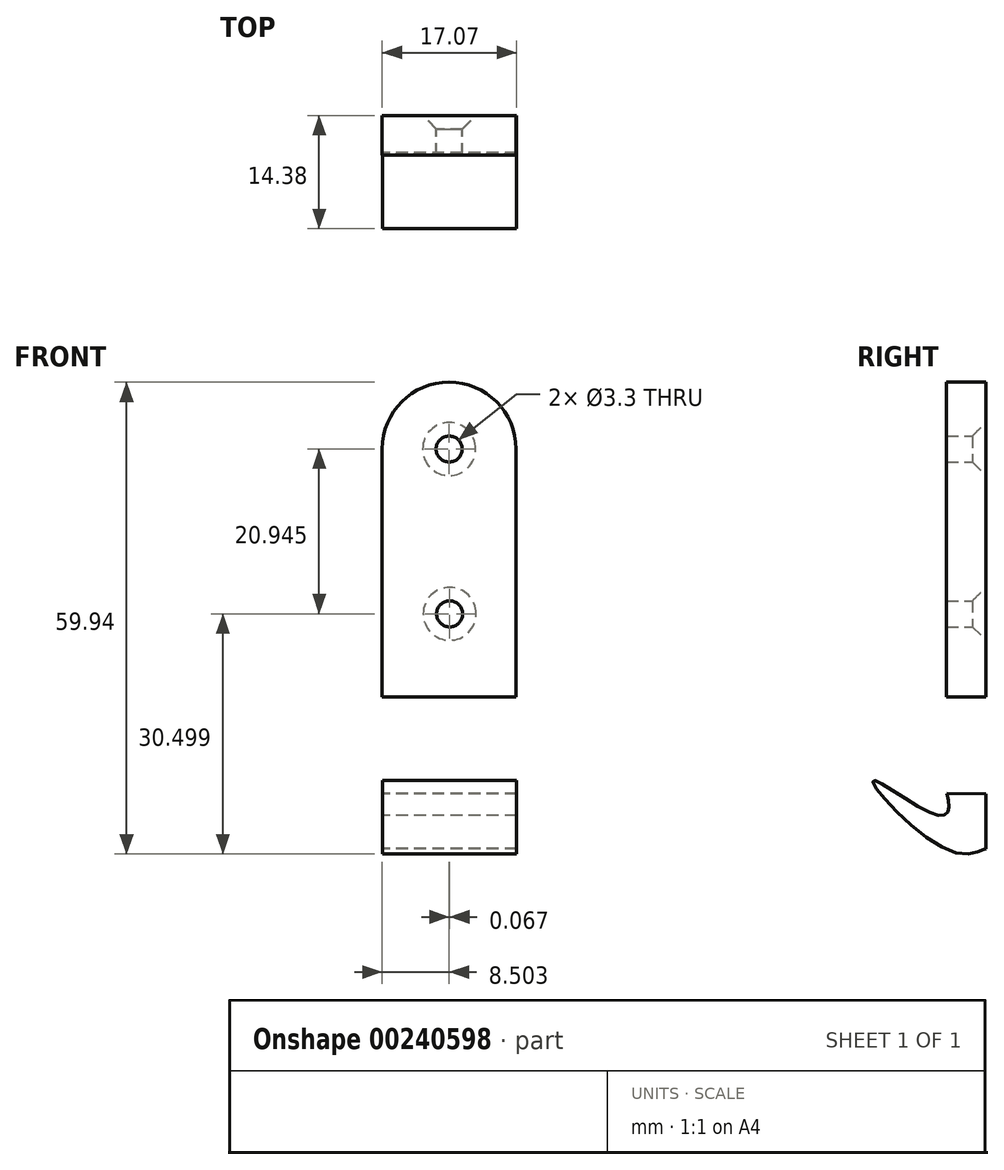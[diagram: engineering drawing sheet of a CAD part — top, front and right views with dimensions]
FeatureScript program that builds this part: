
annotation { "Feature Type Name" : "Feature", "Feature Type Description" : "" }
export const myFeature = defineFeature(function(context is Context, id is Id, definition is map)
    precondition{}
    {
        {
            var Q0;
            Q0=qCreatedBy(makeId("Front.planeOp"),FACE);
            var sketch = newSketch(context, id + "F0", { "sketchPlane" : qUnion([Q0])});
            skLineSegment(sketch, "E0", {"start": v(-8.57, 21.56) * mm, "end": v(-8.57, -9.94) * mm});
            skLineSegment(sketch, "E1", {"start": v(8.43, -9.94) * mm, "end": v(8.43, 21.56) * mm});
            skLineSegment(sketch, "E2", {"start": v(-0.07, 21.56) * mm, "end": v(-0.07, 21.56) * mm});
            skArc(sketch, "E3", {"start": v(8.43, 21.56) * mm, "mid": v(-0.07, 30.06) * mm, "end": v(-8.57, 21.56) * mm});
            skLineSegment(sketch, "E4", {"start": v(-8.57, -9.94) * mm, "end": v(8.43, -9.94) * mm});
            skPoint(sketch, "E5.end.orphan", {"position": v(0, -34.5) * mm});
            skPoint(sketch, "E6", {"position": v(0, 0.62) * mm});
            skSolve(sketch);
        }
        {
            var Q0;
            Q0=makeQuery(id+"F0.imprint","IMPRINT",FACE,{"disambiguationData":[TD([[makeQuery(id+"F0.imprint","IMPRINT",EDGE,{"derivedFrom":sQuery(id+"F0.wireOp",EDGE,"E0")}),1.0]])]});
            var Q1;
            Q1=makeQuery(id+"F0.imprint","IMPRINT",FACE,{"disambiguationData":[TD([[makeQuery(id+"F0.imprint","IMPRINT",EDGE,{"derivedFrom":sQuery(id+"F0.wireOp",EDGE,"E4")}),-1.0]])]});
            extrude(context, id + "F1", {"entities" : qUnion([Q0, Q1]), "depth" : 5 * mm});
        }
        {
            var Q0;
            Q0=qCreatedBy(makeId("Right.planeOp"),FACE);
            var sketch = newSketch(context, id + "F2", { "sketchPlane" : qUnion([Q0])});
            skFitSpline(sketch, "E7", {"points": [v(-4.93, -22.2) * mm, v(-4.84, -24.54) * mm, v(-7.06, -24.63) * mm, v(-14.36, -20.59) * mm, v(-3.88, -29.71) * mm, v(0, -29.2) * mm, v(0, -29.32) * mm], "startDerivative": vector(4.23, -21.43) * mm, "endDerivative": vector(-1.42, -5.42) * mm});
            skLineSegment(sketch, "E8", {"start": v(0.01, -29.27) * mm, "end": v(0.01, -22.23) * mm});
            skLineSegment(sketch, "E9", {"start": v(-4.93, -22.2) * mm, "end": v(0.01, -22.23) * mm});
            skSolve(sketch);
        }
        {
            var Q0;
            {var subQ0=sQuery(id+"F2.wireOp",EDGE,"E9");Q0=makeQuery(id+"F2.imprint","IMPRINT",FACE,{"disambiguationData":[TD([[makeQuery(id+"F2.imprint","IMPRINT",EDGE,{"derivedFrom":subQ0}),-1.0]])]});}
            extrude(context, id + "F3", {"entities" : qUnion([Q0]), "endBound" : BoundingType.SYMMETRIC, "depth" : 17 * mm});
        }
        {
            var Q0;
            Q0=sQuery(id+"F0.wireOp",VERTEX,"E6");
            var Q1;
            Q1=sQuery(id+"F0.wireOp",VERTEX,"E3.center");
            var Q2;
            Q2=makeQuery(id+"F1.opExtrude","SWEPT_BODY",BODY,{"disambiguationData":[OSD([sQuery(id+"F0.wireOp",EDGE,"E0"),sQuery(id+"F0.wireOp",EDGE,"E1"),sQuery(id+"F0.wireOp",EDGE,"E3"),sQuery(id+"F0.wireOp",EDGE,"E4")])]});
            hole(context, id + "F4", {"style" : HoleStyle.C_SINK, "endStyle" : HoleEndStyle.THROUGH, "oppositeDirection" : true, "standardTappedOrClearance" : lookupTablePath({ "fit" : "Normal", "standard" : "ISO", "size" : "M3", "type" : "Clearance" }), "standardBlindInLast" : lookupTablePath({ "fit" : "Standard", "standard" : "ISO", "size" : "M3", "type" : "Clearance" }), "holeDiameter" : 3.3 * mm, "cSinkDiameter" : 6.72 * mm, "cSinkAngle" : 90 * degree, "locations" : qUnion([Q0, Q1]), "scope" : qUnion([Q2]), "isTappedThrough" : true});
        }
    });
